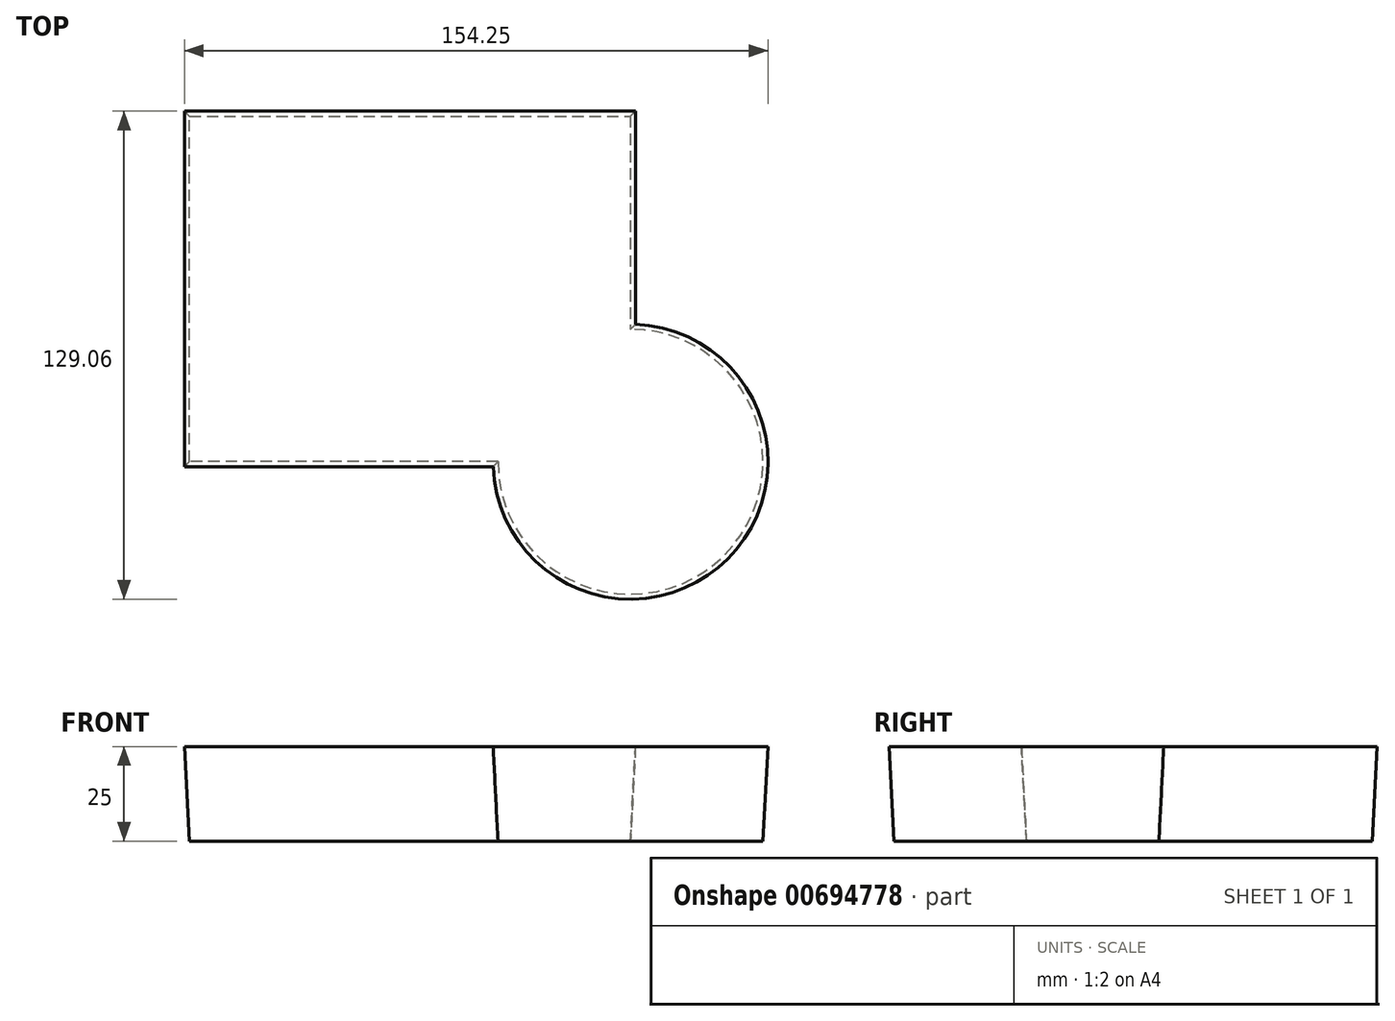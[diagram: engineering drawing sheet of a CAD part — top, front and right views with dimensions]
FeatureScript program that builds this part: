
annotation { "Feature Type Name" : "Feature", "Feature Type Description" : "" }
export const myFeature = defineFeature(function(context is Context, id is Id, definition is map)
    precondition{}
    {
        {
            var Q0;
            Q0=qCreatedBy(makeId("Top.planeOp"),FACE);
            var sketch = newSketch(context, id + "F0", { "sketchPlane" : qUnion([Q0])});
            skLineSegment(sketch, "E0.bottom", {"start": v(-92.88, -39.21) * mm, "end": v(-11.32, -39.21) * mm});
            skLineSegment(sketch, "E0.top", {"start": v(-92.88, 52.2) * mm, "end": v(23.72, 52.2) * mm});
            skLineSegment(sketch, "E0.left", {"start": v(-92.88, -39.21) * mm, "end": v(-92.88, 52.2) * mm});
            skLineSegment(sketch, "E0.right", {"start": v(23.72, -4.18) * mm, "end": v(23.72, 52.2) * mm});
            skArc(sketch, "E1", {"start": v(-11.32, -39.21) * mm, "mid": v(48.49, -63.99) * mm, "end": v(23.72, -4.18) * mm});
            skSolve(sketch);
        }
        {
            var Q0;
            Q0=makeQuery(id+"F0.imprint","IMPRINT",FACE,{"disambiguationData":[TD([[makeQuery(id+"F0.imprint","IMPRINT",EDGE,{"derivedFrom":sQuery(id+"F0.wireOp",EDGE,"E0.bottom")}),1.0]])]});
            extrude(context, id + "F1", {"entities" : qUnion([Q0]), "depth" : 25 * mm, "offsetDistance" : 25 * mm, "hasDraft" : true, "draftAngle" : 3 * degree});
        }
    });
